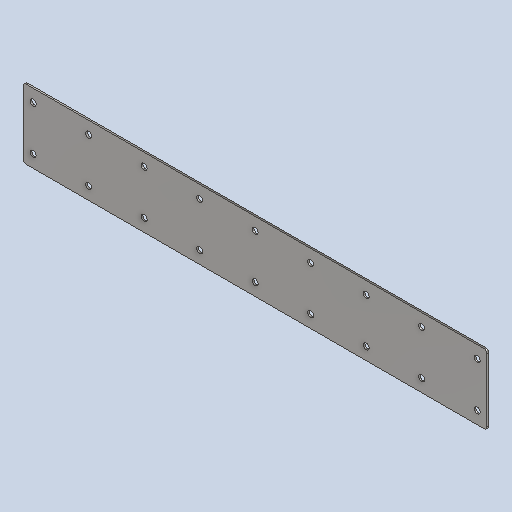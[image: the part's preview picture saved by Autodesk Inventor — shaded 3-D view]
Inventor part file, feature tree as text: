
AUTODESK INVENTOR PART (.ipt)
format: ipt  version: 2022 (Build 260153000, 153)  size: 141,312 bytes
history: native  units: mm
features: sketch x2, other x2, sheet_metal_op x1, pattern_linear x1, fillet x1
ambient origin geometry x8: Origin, YZ Plane, XZ Plane, XY Plane, X Axis, Y Axis, Z Axis, Center Point
bodies: Solid1 (feature_tree)
feature tree (7):
  sheet_metal_op  "Face1"
  pattern_linear  "Rectangular Pattern1"  Spacing1=3.0mm  [1 undecoded]
  fillet  "Fillet1"  Radius=10.7mm
  sketch  "Sketch1"  dims[d0=125.0mm]
  other  "Plate1"
  sketch  "Sketch2"  dims[d1=835.0mm d2=3.0mm d3=10.7mm d4=80.0mm d5=3.0mm d6=0.0mm d7=90.0mm d9=100.0mm d10=5.0mm]
  other  "Cut1"
note: 1 required parameter value undecoded (feature->parameter linkage not recoverable at this tier; creation-order binding heuristic only, values carry confidence <= 0.55)
